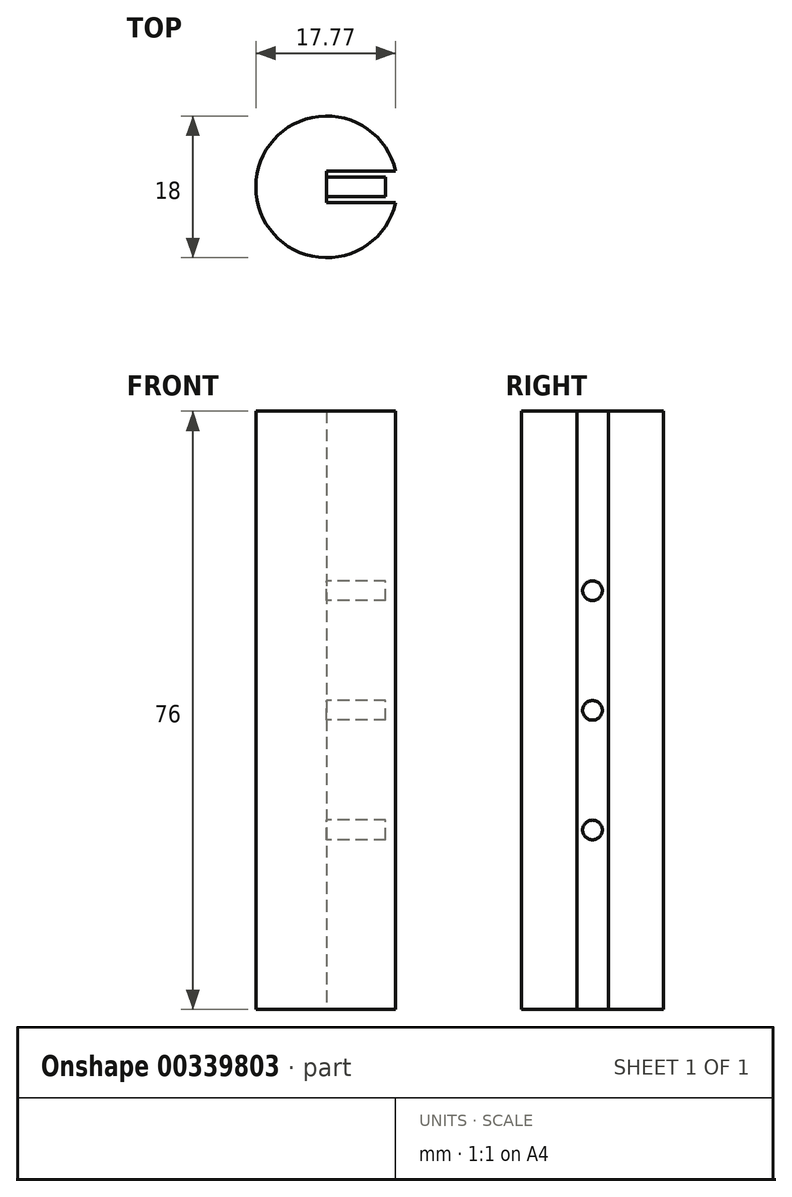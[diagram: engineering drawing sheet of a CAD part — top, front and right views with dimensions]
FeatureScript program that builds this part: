
annotation { "Feature Type Name" : "Feature", "Feature Type Description" : "" }
export const myFeature = defineFeature(function(context is Context, id is Id, definition is map)
    precondition{}
    {
        {
            var Q0;
            Q0=qCreatedBy(makeId("Top.planeOp"),FACE);
            var sketch = newSketch(context, id + "F0", { "sketchPlane" : qUnion([Q0])});
            skCircle(sketch, "E0", {"center": v(0, 2) * mm, "radius": 9 * mm});
            skLineSegment(sketch, "E1", {"start": v(0, 2) * mm, "end": v(0, 4) * mm});
            skLineSegment(sketch, "E2", {"start": v(0, 4) * mm, "end": v(8.77, 4) * mm});
            skLineSegment(sketch, "E3", {"start": v(8.77, 4) * mm, "end": v(0, 4) * mm});
            skLineSegment(sketch, "E4", {"start": v(0, 2) * mm, "end": v(0, 0) * mm});
            skLineSegment(sketch, "E5", {"start": v(0, 0) * mm, "end": v(8.77, 0) * mm});
            skSolve(sketch);
        }
        {
            var Q0;
            Q0=makeQuery(id+"F0.imprint","IMPRINT",FACE,{"disambiguationData":[TD([[makeQuery(id+"F0.imprint","IMPRINT",EDGE,{"derivedFrom":sQuery(id+"F0.wireOp",EDGE,"E1")}),1.0]])]});
            extrude(context, id + "F1", {"entities" : qUnion([Q0]), "depth" : 76 * mm});
        }
        {
            var Q0;
            Q0=makeQuery(id+"F1.opExtrude","SWEPT_FACE",FACE,{"disambiguationData":[OSD([sQuery(id+"F0.wireOp",EDGE,"E1"),sQuery(id+"F0.wireOp",EDGE,"E4")])]});
            var sketch = newSketch(context, id + "F2", { "sketchPlane" : qUnion([Q0])});
            skLineSegment(sketch, "E6", {"start": v(2, 76) * mm, "end": v(2, 58) * mm});
            skLineSegment(sketch, "E7", {"start": v(2, 0) * mm, "end": v(2, 18) * mm});
            skLineSegment(sketch, "E8", {"start": v(2, 58) * mm, "end": v(2, 38) * mm});
            skLineSegment(sketch, "E9", {"start": v(2, 38) * mm, "end": v(2, 18) * mm});
            skCircle(sketch, "E10", {"center": v(2, 38) * mm, "radius": 1.25 * mm});
            skLineSegment(sketch, "E11", {"start": v(2, 39.25) * mm, "end": v(2, 51.95) * mm});
            skLineSegment(sketch, "E12", {"start": v(2, 36.75) * mm, "end": v(2, 24.05) * mm});
            skLineSegment(sketch, "E13", {"start": v(2, 51.95) * mm, "end": v(2, 53.2) * mm});
            skLineSegment(sketch, "E14", {"start": v(2, 24.05) * mm, "end": v(2, 22.8) * mm});
            skCircle(sketch, "E15", {"center": v(2, 53.2) * mm, "radius": 1.25 * mm});
            skCircle(sketch, "E16", {"center": v(2, 22.8) * mm, "radius": 1.25 * mm});
            skSolve(sketch);
        }
        {
            var Q0;
            Q0 = qSketchRegion(id + "F2", true);
            extrude(context, id + "F3", {"entities" : qUnion([Q0]), "operationType" : NewBodyOperationType.ADD, "depth" : 7.5 * mm});
        }
    });
